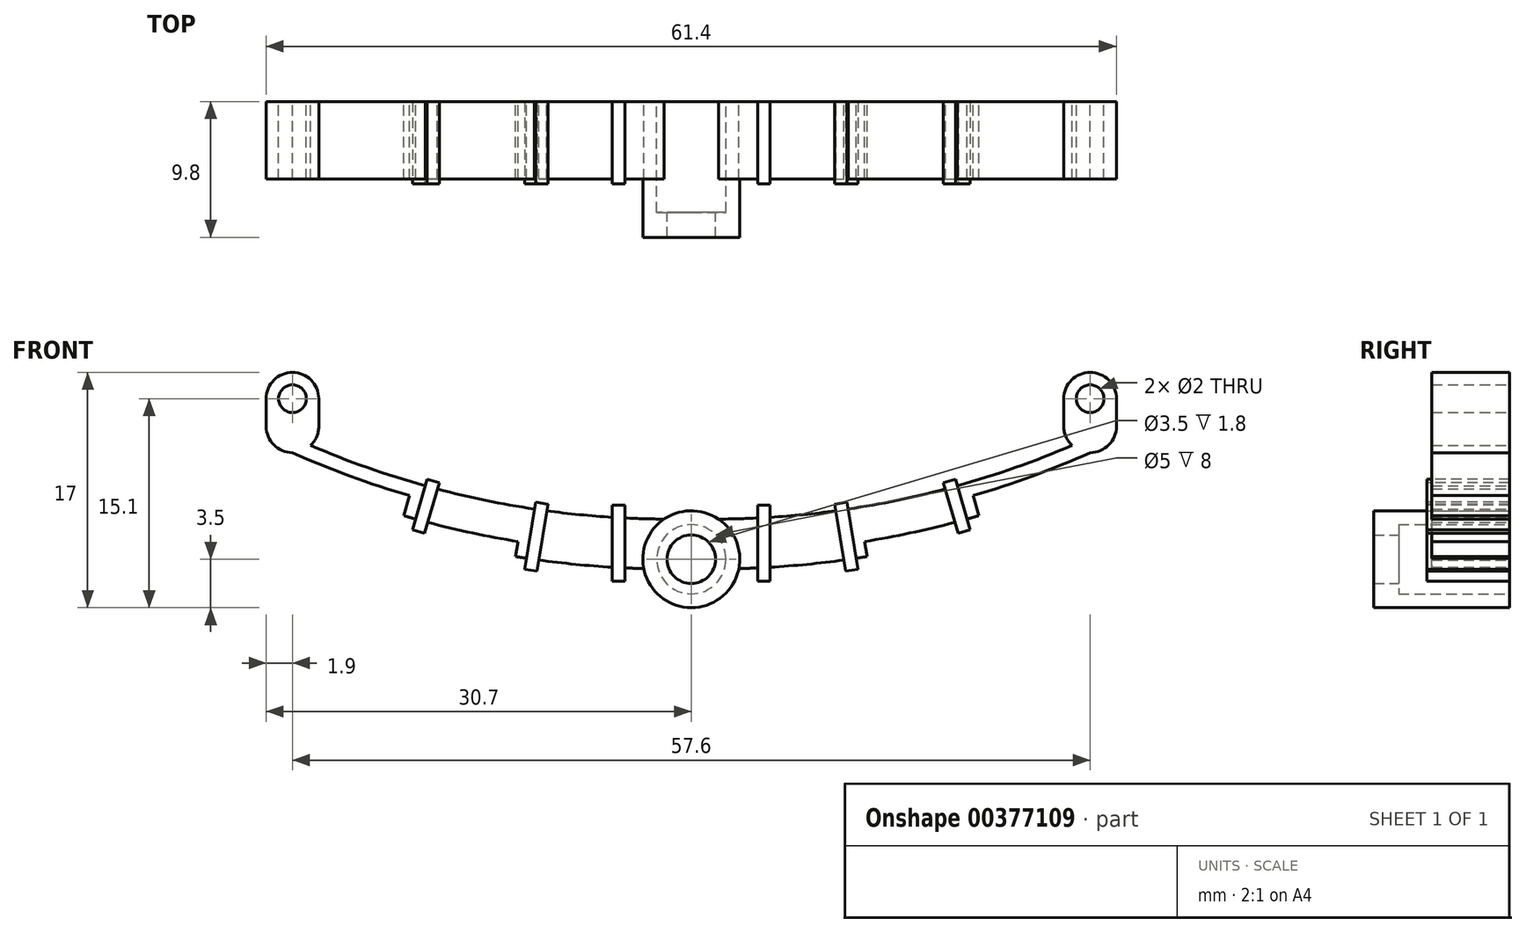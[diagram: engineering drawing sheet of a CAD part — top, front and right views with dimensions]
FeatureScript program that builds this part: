
annotation { "Feature Type Name" : "Feature", "Feature Type Description" : "" }
export const myFeature = defineFeature(function(context is Context, id is Id, definition is map)
    precondition{}
    {
        {
            var Q0;
            Q0=qCreatedBy(makeId("Front.planeOp"),FACE);
            var sketch = newSketch(context, id + "F0", { "sketchPlane" : qUnion([Q0])});
            skArc(sketch, "E0", {"start": v(-26.9, 0) * mm, "mid": v(-28.8, 1.9) * mm, "end": v(-30.7, 0) * mm});
            skArc(sketch, "E1", {"start": v(-30.7, -2) * mm, "mid": v(-30.14, -3.34) * mm, "end": v(-28.8, -3.9) * mm});
            skLineSegment(sketch, "E2", {"start": v(-30.7, 0) * mm, "end": v(-30.7, -2) * mm});
            skLineSegment(sketch, "E3", {"start": v(-26.9, 0) * mm, "end": v(-26.9, -2) * mm});
            skCircle(sketch, "E4", {"center": v(-28.8, 0) * mm, "radius": 1 * mm});
            skCircle(sketch, "E5", {"center": v(0, -11.6) * mm, "radius": 1.75 * mm});
            skPoint(sketch, "E6", {"position": v(-28.8, -3.9) * mm});
            skLineSegment(sketch, "E7", {"start": v(0, -8.7) * mm, "end": v(-1.6, -8.7) * mm, "construction": true});
            skArc(sketch, "E8", {"start": v(-27.5, -3.38) * mm, "mid": v(-15, -7.32) * mm, "end": v(-1.96, -8.7) * mm});
            skArc(sketch, "E9.0", {"start": v(-28.8, -3.9) * mm, "mid": v(-24.63, -5.6) * mm, "end": v(-20.35, -7) * mm});
            skArc(sketch, "E10.trimOffspring", {"start": v(-27.5, -3.38) * mm, "mid": v(-27.05, -2.75) * mm, "end": v(-26.9, -2) * mm});
            skLineSegment(sketch, "E11", {"start": v(-1.6, 56.98) * mm, "end": v(-20.35, -7) * mm, "construction": true});
            skLineSegment(sketch, "E12", {"start": v(-20.35, -7) * mm, "end": v(-20.78, -8.45) * mm});
            skArc(sketch, "E13.0", {"start": v(-20.78, -8.45) * mm, "mid": v(-16.68, -9.51) * mm, "end": v(-12.52, -10.32) * mm});
            skLineSegment(sketch, "E14", {"start": v(-1.6, 56.98) * mm, "end": v(-12.52, -10.32) * mm, "construction": true});
            skLineSegment(sketch, "E15", {"start": v(-12.52, -10.32) * mm, "end": v(-12.7, -11.4) * mm});
            skArc(sketch, "E16.0", {"start": v(-12.7, -11.4) * mm, "mid": v(-8.08, -12) * mm, "end": v(-3.43, -12.28) * mm});
            skArc(sketch, "E17", {"start": v(-3.43, -12.28) * mm, "mid": v(0, -15.1) * mm, "end": v(3.43, -12.28) * mm});
            skLineSegment(sketch, "E18.MirrorCS", {"start": v(12.52, -10.32) * mm, "end": v(12.7, -11.4) * mm});
            skLineSegment(sketch, "E19.MirrorCS", {"start": v(30.7, 0) * mm, "end": v(30.7, -2) * mm});
            skArc(sketch, "E20.MirrorCS", {"start": v(30.7, -2) * mm, "mid": v(30.14, -3.34) * mm, "end": v(28.8, -3.9) * mm});
            skArc(sketch, "E21.MirrorCS", {"start": v(20.78, -8.45) * mm, "mid": v(16.68, -9.51) * mm, "end": v(12.52, -10.32) * mm});
            skLineSegment(sketch, "E22.MirrorCS", {"start": v(26.9, 0) * mm, "end": v(26.9, -2) * mm});
            skArc(sketch, "E23.MirrorCS", {"start": v(27.5, -3.38) * mm, "mid": v(27.05, -2.75) * mm, "end": v(26.9, -2) * mm});
            skArc(sketch, "E24.MirrorCS", {"start": v(26.9, 0) * mm, "mid": v(28.8, 1.9) * mm, "end": v(30.7, 0) * mm});
            skArc(sketch, "E25.MirrorCS", {"start": v(28.8, -3.9) * mm, "mid": v(24.63, -5.6) * mm, "end": v(20.35, -7) * mm});
            skLineSegment(sketch, "E26.MirrorCS", {"start": v(20.35, -7) * mm, "end": v(20.78, -8.45) * mm});
            skPoint(sketch, "E27.MirrorP", {"position": v(28.8, -3.9) * mm});
            skCircle(sketch, "E28.MirrorC", {"center": v(28.8, 0) * mm, "radius": 1 * mm});
            skArc(sketch, "E29.MirrorCS", {"start": v(27.5, -3.38) * mm, "mid": v(15, -7.32) * mm, "end": v(1.96, -8.7) * mm});
            skArc(sketch, "E30.MirrorCS", {"start": v(12.7, -11.4) * mm, "mid": v(8.08, -12) * mm, "end": v(3.43, -12.28) * mm});
            skArc(sketch, "E31", {"start": v(-3.43, -12.28) * mm, "mid": v(3.24, -12.94) * mm, "end": v(-1.96, -8.7) * mm});
            skPoint(sketch, "E32.MirrorCS.start.orphan", {"position": v(0, -8.7) * mm});
            skSolve(sketch);
        }
        {
            var Q0;
            Q0 = qSketchRegion(id + "F0", true);
            extrude(context, id + "F1", {"entities" : qUnion([Q0]), "depth" : 5.6 * mm});
        }
        {
            var Q0;
            Q0=qCreatedBy(makeId("Front.planeOp"),FACE);
            cPlane(context, id + "F2", {"entities" : qUnion([Q0]), "cplaneType" : CPlaneType.OFFSET, "offset" : (5.6 + 0.35) * mm, "width" : 150 * mm, "height" : 150 * mm});
        }
        {
            var Q0;
            Q0=qCreatedBy(id+"F2.planeOp",FACE);
            var sketch = newSketch(context, id + "F3", { "sketchPlane" : qUnion([Q0])});
            skLineSegment(sketch, "E33.bottom", {"start": v(-19.07, -5.82) * mm, "end": v(-18.2, -6.08) * mm});
            skLineSegment(sketch, "E33.top", {"start": v(-20.14, -9.47) * mm, "end": v(-19.27, -9.72) * mm});
            skLineSegment(sketch, "E33.left", {"start": v(-19.07, -5.82) * mm, "end": v(-20.14, -9.47) * mm});
            skLineSegment(sketch, "E33.right", {"start": v(-18.2, -6.08) * mm, "end": v(-19.27, -9.72) * mm});
            skLineSegment(sketch, "E34.bottom", {"start": v(-11.25, -7.49) * mm, "end": v(-10.36, -7.63) * mm});
            skLineSegment(sketch, "E34.top", {"start": v(-12.03, -12.32) * mm, "end": v(-11.15, -12.47) * mm});
            skLineSegment(sketch, "E34.left", {"start": v(-11.25, -7.49) * mm, "end": v(-12.03, -12.32) * mm});
            skLineSegment(sketch, "E34.right", {"start": v(-10.36, -7.63) * mm, "end": v(-11.15, -12.47) * mm});
            skLineSegment(sketch, "E35.bottom", {"start": v(-5.7, -7.7) * mm, "end": v(-4.8, -7.7) * mm});
            skLineSegment(sketch, "E35.top", {"start": v(-5.7, -13.2) * mm, "end": v(-4.8, -13.2) * mm});
            skLineSegment(sketch, "E35.left", {"start": v(-5.7, -7.7) * mm, "end": v(-5.7, -13.2) * mm});
            skLineSegment(sketch, "E35.right", {"start": v(-4.8, -7.7) * mm, "end": v(-4.8, -13.2) * mm});
            skLineSegment(sketch, "E36.MirrorCS", {"start": v(5.7, -13.2) * mm, "end": v(4.8, -13.2) * mm});
            skLineSegment(sketch, "E37.MirrorCS", {"start": v(5.7, -7.7) * mm, "end": v(4.8, -7.7) * mm});
            skLineSegment(sketch, "E38.MirrorCS", {"start": v(12.03, -12.32) * mm, "end": v(11.15, -12.47) * mm});
            skLineSegment(sketch, "E39.MirrorCS", {"start": v(19.07, -5.82) * mm, "end": v(18.2, -6.08) * mm});
            skLineSegment(sketch, "E40.MirrorCS", {"start": v(20.14, -9.47) * mm, "end": v(19.27, -9.72) * mm});
            skLineSegment(sketch, "E41.MirrorCS", {"start": v(11.25, -7.49) * mm, "end": v(10.36, -7.63) * mm});
            skLineSegment(sketch, "E42.MirrorCS", {"start": v(4.8, -7.7) * mm, "end": v(4.8, -13.2) * mm});
            skLineSegment(sketch, "E43.MirrorCS", {"start": v(5.7, -7.7) * mm, "end": v(5.7, -13.2) * mm});
            skLineSegment(sketch, "E44.MirrorCS", {"start": v(10.36, -7.63) * mm, "end": v(11.15, -12.47) * mm});
            skLineSegment(sketch, "E45.MirrorCS", {"start": v(11.25, -7.49) * mm, "end": v(12.03, -12.32) * mm});
            skLineSegment(sketch, "E46.MirrorCS", {"start": v(19.07, -5.82) * mm, "end": v(20.14, -9.47) * mm});
            skLineSegment(sketch, "E47.MirrorCS", {"start": v(18.2, -6.08) * mm, "end": v(19.27, -9.72) * mm});
            skSolve(sketch);
        }
        {
            var Q0;
            Q0 = qSketchRegion(id + "F3", true);
            var Q1;
            Q1=qCreatedBy(makeId("Front.planeOp"),FACE);
            extrude(context, id + "F4", {"entities" : qUnion([Q0]), "operationType" : NewBodyOperationType.ADD, "endBound" : BoundingType.UP_TO_SURFACE, "oppositeDirection" : true, "endBoundEntityFace" : qUnion([Q1]), "depth" : 25 * mm});
        }
        {
            var Q0;
            {var subQ0=sQuery(id+"F0.wireOp",EDGE,"E29.MirrorCS");var subQ1=sQuery(id+"F0.wireOp",EDGE,"E16.0");var subQ2=sQuery(id+"F0.wireOp",EDGE,"E8");var subQ3=sQuery(id+"F0.wireOp",EDGE,"E5");var subQ4=sQuery(id+"F0.wireOp",EDGE,"E30.MirrorCS");var subQ5=sQuery(id+"F0.wireOp",EDGE,"E31");Q0=makeQuery(id+"F4.boolean.opBoolean","SPLIT",FACE,{"disambiguationData":[TD([makeQuery(id+"F1.opExtrude","SWEPT_FACE",FACE,{"disambiguationData":[OSD([subQ3])]})])],"derivedFrom":makeQuery(id+"F1.opExtrude","CAP_FACE",FACE,{"disambiguationData":[OSD([sQuery(id+"F0.wireOp",EDGE,"E0"),sQuery(id+"F0.wireOp",EDGE,"E1"),sQuery(id+"F0.wireOp",EDGE,"E2"),sQuery(id+"F0.wireOp",EDGE,"E3"),sQuery(id+"F0.wireOp",EDGE,"E4"),subQ3,subQ2,sQuery(id+"F0.wireOp",EDGE,"E9.0"),sQuery(id+"F0.wireOp",EDGE,"E10.trimOffspring"),sQuery(id+"F0.wireOp",EDGE,"E12"),sQuery(id+"F0.wireOp",EDGE,"E13.0"),sQuery(id+"F0.wireOp",EDGE,"E15"),subQ1,sQuery(id+"F0.wireOp",EDGE,"E18.MirrorCS"),sQuery(id+"F0.wireOp",EDGE,"E19.MirrorCS"),sQuery(id+"F0.wireOp",EDGE,"E20.MirrorCS"),sQuery(id+"F0.wireOp",EDGE,"E21.MirrorCS"),sQuery(id+"F0.wireOp",EDGE,"E22.MirrorCS"),sQuery(id+"F0.wireOp",EDGE,"E23.MirrorCS"),sQuery(id+"F0.wireOp",EDGE,"E24.MirrorCS"),sQuery(id+"F0.wireOp",EDGE,"E25.MirrorCS"),sQuery(id+"F0.wireOp",EDGE,"E26.MirrorCS"),sQuery(id+"F0.wireOp",EDGE,"E28.MirrorC"),subQ0,subQ4,subQ5])],"isStart":false})});}
            var sketch = newSketch(context, id + "F5", { "sketchPlane" : qUnion([Q0])});
            skCircle(sketch, "E48.0", {"center": v(0, -11.6) * mm, "radius": 1.75 * mm});
            skCircle(sketch, "E49", {"center": v(0, -11.6) * mm, "radius": 3.5 * mm});
            skSolve(sketch);
        }
        {
            var Q0;
            Q0 = qSketchRegion(id + "F5", true);
            extrude(context, id + "F6", {"entities" : qUnion([Q0]), "operationType" : NewBodyOperationType.ADD, "depth" : 4.2 * mm});
        }
        {
            var Q0;
            {var subQ0=dummyQuery(id+"Front.planeOp",FACE);Q0=makeQuery(id+"F4.boolean.opBoolean","MERGE",FACE,{"derivedFrom":[makeQuery(id+"F1.opExtrude","CAP_FACE",FACE,{"disambiguationData":[OSD([sQuery(id+"F0.wireOp",EDGE,"E0"),sQuery(id+"F0.wireOp",EDGE,"E1"),sQuery(id+"F0.wireOp",EDGE,"E2"),sQuery(id+"F0.wireOp",EDGE,"E3"),sQuery(id+"F0.wireOp",EDGE,"E4"),sQuery(id+"F0.wireOp",EDGE,"E5"),sQuery(id+"F0.wireOp",EDGE,"E8"),sQuery(id+"F0.wireOp",EDGE,"E9.0"),sQuery(id+"F0.wireOp",EDGE,"E10.trimOffspring"),sQuery(id+"F0.wireOp",EDGE,"E12"),sQuery(id+"F0.wireOp",EDGE,"E13.0"),sQuery(id+"F0.wireOp",EDGE,"E15"),sQuery(id+"F0.wireOp",EDGE,"E16.0"),sQuery(id+"F0.wireOp",EDGE,"E18.MirrorCS"),sQuery(id+"F0.wireOp",EDGE,"E19.MirrorCS"),sQuery(id+"F0.wireOp",EDGE,"E20.MirrorCS"),sQuery(id+"F0.wireOp",EDGE,"E21.MirrorCS"),sQuery(id+"F0.wireOp",EDGE,"E22.MirrorCS"),sQuery(id+"F0.wireOp",EDGE,"E23.MirrorCS"),sQuery(id+"F0.wireOp",EDGE,"E24.MirrorCS"),sQuery(id+"F0.wireOp",EDGE,"E25.MirrorCS"),sQuery(id+"F0.wireOp",EDGE,"E26.MirrorCS"),sQuery(id+"F0.wireOp",EDGE,"E28.MirrorC"),sQuery(id+"F0.wireOp",EDGE,"E29.MirrorCS"),sQuery(id+"F0.wireOp",EDGE,"E30.MirrorCS"),sQuery(id+"F0.wireOp",EDGE,"E31")])],"isStart":true}),makeQuery(id+"F4.opExtrude","CAP_FACE",FACE,{"disambiguationData":[OSD([subQ0]),ownerDisambiguation([makeQuery(id+"F3.imprint","IMPRINT",EDGE,{"derivedFrom":sQuery(id+"F3.wireOp",EDGE,"E33.bottom")})])],"isStart":false}),makeQuery(id+"F4.opExtrude","CAP_FACE",FACE,{"disambiguationData":[OSD([subQ0]),ownerDisambiguation([makeQuery(id+"F3.imprint","IMPRINT",EDGE,{"derivedFrom":sQuery(id+"F3.wireOp",EDGE,"E34.bottom")})])],"isStart":false}),makeQuery(id+"F4.opExtrude","CAP_FACE",FACE,{"disambiguationData":[OSD([subQ0]),ownerDisambiguation([makeQuery(id+"F3.imprint","IMPRINT",EDGE,{"derivedFrom":sQuery(id+"F3.wireOp",EDGE,"E35.bottom")})])],"isStart":false}),makeQuery(id+"F4.opExtrude","CAP_FACE",FACE,{"disambiguationData":[OSD([subQ0]),ownerDisambiguation([makeQuery(id+"F3.imprint","IMPRINT",EDGE,{"derivedFrom":sQuery(id+"F3.wireOp",EDGE,"E36.MirrorCS")})])],"isStart":false}),makeQuery(id+"F4.opExtrude","CAP_FACE",FACE,{"disambiguationData":[OSD([subQ0]),ownerDisambiguation([makeQuery(id+"F3.imprint","IMPRINT",EDGE,{"derivedFrom":sQuery(id+"F3.wireOp",EDGE,"E38.MirrorCS")})])],"isStart":false}),makeQuery(id+"F4.opExtrude","CAP_FACE",FACE,{"disambiguationData":[OSD([subQ0]),ownerDisambiguation([makeQuery(id+"F3.imprint","IMPRINT",EDGE,{"derivedFrom":sQuery(id+"F3.wireOp",EDGE,"E39.MirrorCS")})])],"isStart":false})]});}
            var sketch = newSketch(context, id + "F7", { "sketchPlane" : qUnion([Q0])});
            skCircle(sketch, "E50", {"center": v(0, -11.6) * mm, "radius": 2.5 * mm});
            skSolve(sketch);
        }
        {
            var Q0;
            Q0 = qSketchRegion(id + "F7", true);
            extrude(context, id + "F8", {"entities" : qUnion([Q0]), "operationType" : NewBodyOperationType.REMOVE, "oppositeDirection" : true, "depth" : 8 * mm});
        }
    });
